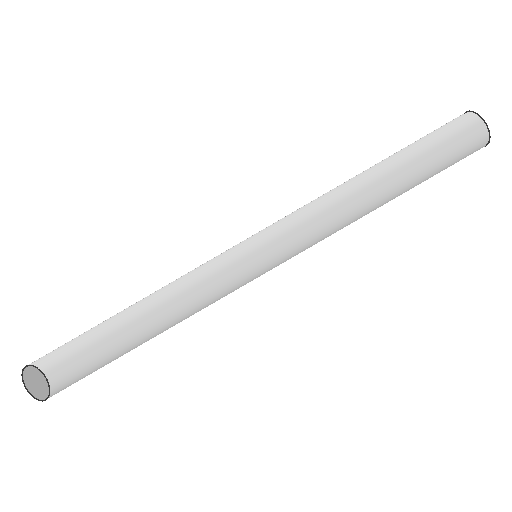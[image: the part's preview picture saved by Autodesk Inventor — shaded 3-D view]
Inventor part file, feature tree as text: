
AUTODESK INVENTOR PART (.ipt)
format: ipt  version: 2025.2 (Build 292293000, 293)  size: 79,872 bytes
history: native  units: in
note: dims shown in document units (in); Inventor stores cm internally (conversion verified against a paired STEP export)
features: extrude x1, sketch x1
ambient origin geometry x8: Origin, YZ Plane, XZ Plane, XY Plane, X Axis, Y Axis, Z Axis, Center Point
bodies: Solid1 (feature_tree)
feature tree (2):
  extrude  "Extrusion1"  Depth=5.0in TaperAngle=0.0deg
  sketch  "Sketch1"  dims[d0=0.315in d1=5.0in d2=0.0in]
